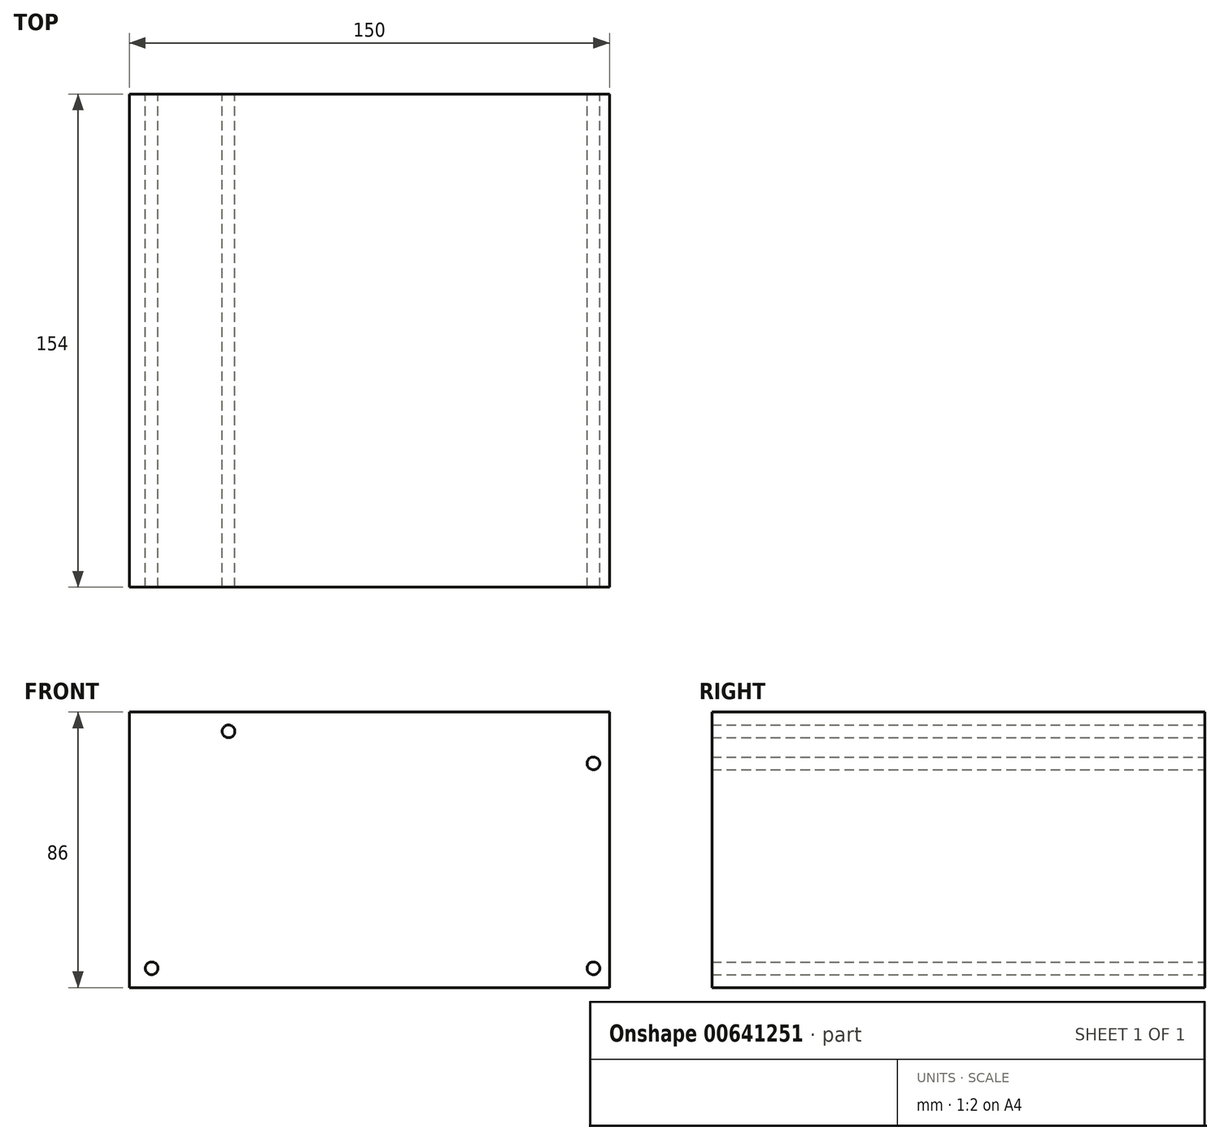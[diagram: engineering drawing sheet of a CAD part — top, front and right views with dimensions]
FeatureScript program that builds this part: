
annotation { "Feature Type Name" : "Feature", "Feature Type Description" : "" }
export const myFeature = defineFeature(function(context is Context, id is Id, definition is map)
    precondition{}
    {
        {
            var Q0;
            Q0=qCreatedBy(makeId("Front.planeOp"),FACE);
            var sketch = newSketch(context, id + "F0", { "sketchPlane" : qUnion([Q0])});
            skLineSegment(sketch, "E0.bottom", {"start": v(-75.03, -34.57) * mm, "end": v(74.97, -34.57) * mm});
            skLineSegment(sketch, "E0.top", {"start": v(-75.03, 51.43) * mm, "end": v(74.97, 51.43) * mm});
            skLineSegment(sketch, "E0.left", {"start": v(-75.03, -34.57) * mm, "end": v(-75.03, 51.43) * mm});
            skLineSegment(sketch, "E0.right", {"start": v(74.97, -34.57) * mm, "end": v(74.97, 51.43) * mm});
            skCircle(sketch, "E1", {"center": v(-44.03, 45.43) * mm, "radius": 2 * mm});
            skCircle(sketch, "E2", {"center": v(69.97, 35.43) * mm, "radius": 2 * mm});
            skCircle(sketch, "E3", {"center": v(69.97, -28.57) * mm, "radius": 2 * mm});
            skCircle(sketch, "E4", {"center": v(-68.03, -28.57) * mm, "radius": 2 * mm});
            skSolve(sketch);
        }
        {
            var Q0;
            Q0=makeQuery(id+"F0.imprint","IMPRINT",FACE,{"disambiguationData":[TD([[makeQuery(id+"F0.imprint","IMPRINT",EDGE,{"derivedFrom":sQuery(id+"F0.wireOp",EDGE,"E0.bottom")}),1.0]])]});
            extrude(context, id + "F1", {"entities" : qUnion([Q0]), "depth" : 154 * mm, "offsetDistance" : 25 * mm});
        }
    });
